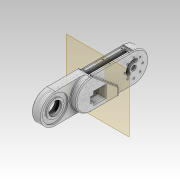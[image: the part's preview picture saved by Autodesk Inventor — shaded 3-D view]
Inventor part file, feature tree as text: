
AUTODESK INVENTOR PART (.ipt)
format: ipt  version: 2020 (Build 240168000, 168)  size: 705,536 bytes
history: native  units: mm
features: sketch x28, extrude x26, fillet x3, plane x2, revolve x2, projected_geometry x1
ambient origin geometry x8: Origin, YZ Plane, XZ Plane, XY Plane, X Axis, Y Axis, Z Axis, Center Point
bodies: Solid1 (feature_tree)
feature tree (62):
  extrude  "Extrusion1"  Depth=250.0mm
  extrude  "Extrusion3"  Depth=50.0mm TaperAngle=0.0deg
  extrude  "Extrusion6"  TaperAngle=0.0deg  [1 undecoded]
  extrude  "Extrusion7"  Depth=50.0mm
  extrude  "Extrusion8"  Depth=10.0mm TaperAngle=0.0deg
  extrude  "Extrusion9"  TaperAngle=0.0deg  [1 undecoded]
  extrude  "Extrusion10"  TaperAngle=30.0deg  [1 undecoded]
  extrude  "Extrusion11"  Depth=16.15mm
  extrude  "Extrusion12"  Depth=60.0mm
  plane  "Work Plane1"
  extrude  "Extrusion13"  Depth=10.0mm TaperAngle=0.0deg
  revolve  "Revolution1"  [1 undecoded]
  extrude  "Extrusion14"  Depth=86.0mm
  extrude  "Extrusion15"  Depth=4.0mm TaperAngle=0.0deg
  extrude  "Extrusion16"  Depth=70.0mm
  revolve  "Revolution2"  [1 undecoded]
  extrude  "Extrusion17"  Depth=7.3mm
  fillet  "Fillet1"  [1 undecoded]
  plane  "Work Plane2"
  extrude  "Extrusion18"  Depth=34.0mm
  extrude  "Extrusion19"  Depth=3.0mm TaperAngle=0.0deg
  extrude  "Extrusion20"  Depth=15.0mm TaperAngle=0.0deg
  extrude  "Extrusion21"  Depth=130.0mm
  extrude  "Extrusion25"  Depth=6.0mm TaperAngle=360.0deg
  extrude  "Extrusion22"  Depth=1.0mm
  fillet  "Fillet2"  Radius=5.2mm
  fillet  "Fillet3"  Radius=1.0mm
  extrude  "Extrusion23"  TaperAngle=90.0deg  [1 undecoded]
  extrude  "Extrusion24"  Depth=20.0mm
  extrude  "Extrusion26"  Depth=19.198622mm
  extrude  "Extrusion27"  Depth=50.0mm
  extrude  "Extrusion28"  TaperAngle=0.0deg  [1 undecoded]
  extrude  "CHOP"  Depth=12.0mm
  sketch  "Sketch1"  dims[d0=50.0mm d1=250.0mm]
  sketch  "Sketch3"  dims[d2=47.2mm d3=50.0mm d4=0.0mm]
  sketch  "Sketch6"  dims[d10=5.0mm d11=0.0mm d12=0.0mm]
  sketch  "Sketch7"  dims[d19=50.0mm d20=0.0mm d21=8.726646mm]
  projected_geometry  "Projected Loop1"
  sketch  "Sketch8"  dims[d22=75.0mm d25=10.0mm d26=0.0mm]
  sketch  "Sketch9"  dims[d27=50.0mm d30=0.0mm d31=0.0mm]
  sketch  "Sketch10"  dims[d33=30.0deg d34=30.0deg]
  sketch  "Sketch11"  dims[d35=0.0mm d36=0.0mm d37=16.15mm]
  sketch  "Sketch12"  dims[d38=3.3mm d39=60.0mm]
  sketch  "Sketch13"  dims[d40=80.0mm d42=360.0deg d44=10.0mm d45=0.0mm]
  sketch  "Sketch14"  dims[d50=42.0mm d51=42.0mm d52=0.0mm d53=0.0mm]
  sketch  "Sketch15"  dims[d54=38.0mm d55=86.0mm]
  sketch  "Sketch16"  dims[d56=59.0mm d57=4.0mm d58=0.0mm]
  sketch  "Sketch17"  dims[d59=-2.0mm d60=70.0mm]
  sketch  "Sketch18"  dims[d61=40.0mm d62=18.0mm d63=0.0mm]
  sketch  "Sketch19"  dims[d64=1.5mm d65=7.3mm d66=90.0deg]
  sketch  "Sketch20"  dims[d67=22.0mm d68=34.0mm]
  sketch  "Sketch21"  dims[d69=3.5mm d70=3.0mm d71=0.0mm]
  sketch  "Sketch22"  dims[d72=0.0mm d73=15.0mm d74=0.0mm]
  sketch  "Sketch23"  dims[d75=15.0mm d76=130.0mm]
  sketch  "Sketch24"  dims[d77=6.0mm d78=80.0mm d80=360.0deg]
  sketch  "Sketch25"  dims[d82=15.0mm d83=0.0mm d84=5.2mm d85=5.2mm d86=1.0mm]
  sketch  "Sketch26"  dims[d87=1.5mm d88=90.0deg]
  sketch  "Sketch27"  dims[d89=5.5mm d90=20.0mm]
  sketch  "Sketch28"  dims[d91=30.0deg d92=19.198622mm]
  sketch  "Sketch29"  dims[d93=15.0mm d94=0.0mm d95=50.0mm]
  sketch  "Sketch30"  dims[d96=30.0mm d97=0.0mm]
  sketch  "Sketch31"  dims[d98=8.0mm d99=12.0mm d100=6.1mm d101=13.0mm d102=125.0mm d103=75.0mm d104=0.0mm d105=0.0mm d106=2.1mm d107=10.0mm d108=10.0mm d109=32.0mm d110=110.0mm d111=0.0mm d112=3.0mm d113=3.0mm d114=5.0mm d115=1.0mm d116=4.0mm d117=0.0mm d118=4.0mm d119=4.0mm d120=32.25mm d121=0.0mm d122=3.0mm d124=0.5mm d125=0.0mm d126=3.0mm d127=2.0mm d128=8.0mm d129=8.0mm d130=4.0mm d131=4.0mm d132=3.9mm d133=6.0mm d134=0.0mm d135=4.0mm d136=0.0mm d137=60.0mm d138=0.5mm d139=0.0mm d140=3.0mm d141=10.0mm d142=20.0mm d143=15.0mm d144=0.0mm d145=8.0mm d146=23.75mm d147=0.0mm d148=15.0mm d149=23.75mm d150=0.0mm d151=200.998mm d152=0.0mm d123=0.872665mm]
note: 8 required parameter values undecoded (feature->parameter linkage not recoverable at this tier; creation-order binding heuristic only, values carry confidence <= 0.55)